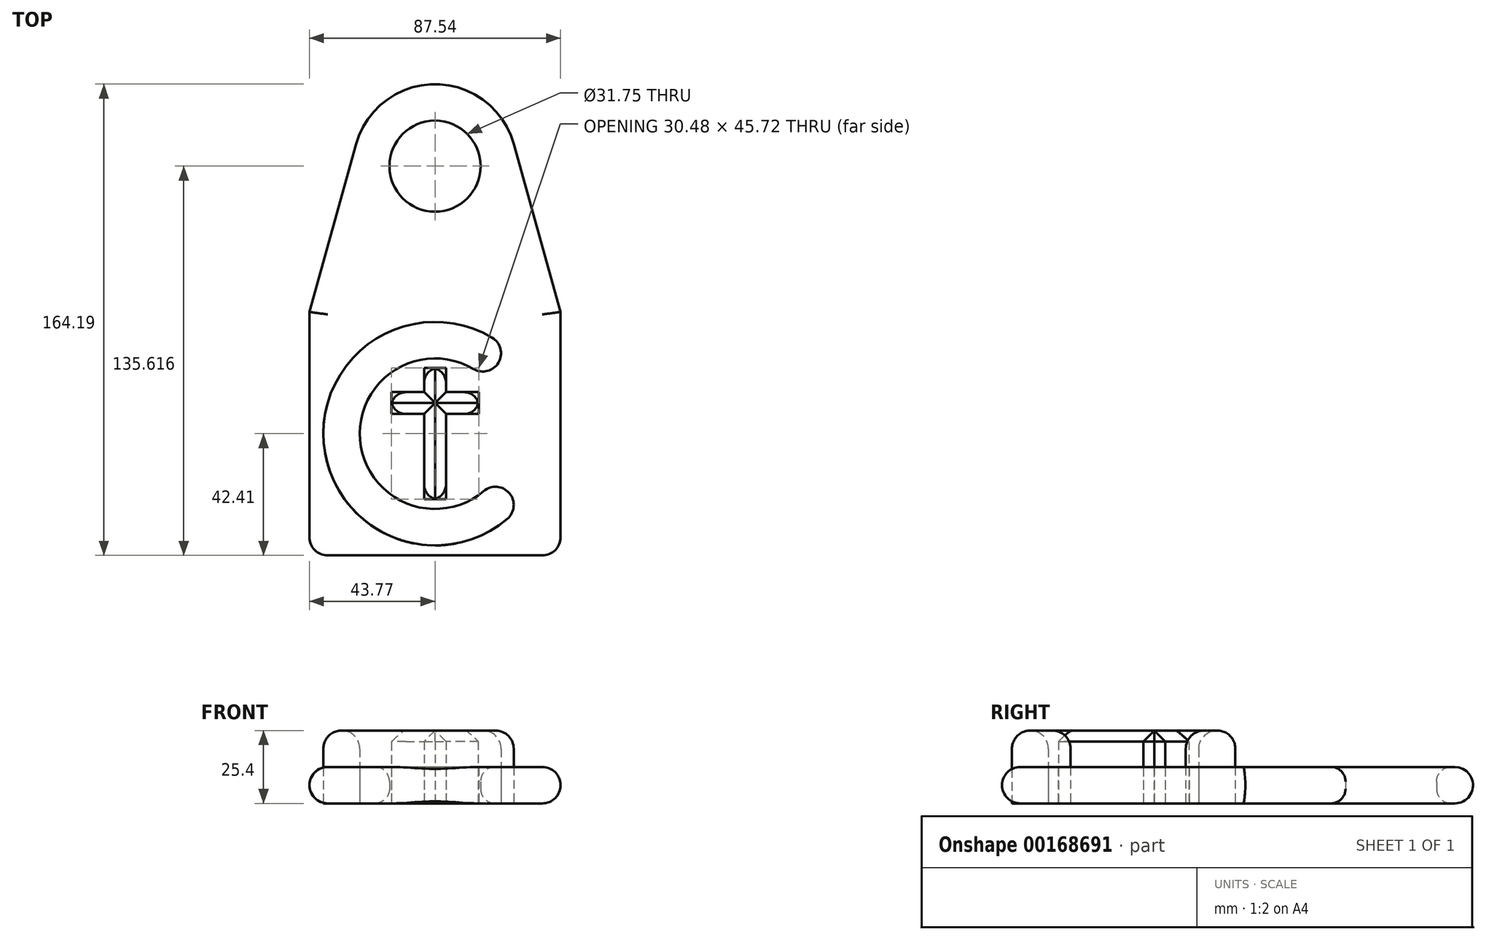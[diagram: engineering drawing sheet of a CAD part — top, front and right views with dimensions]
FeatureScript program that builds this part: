
annotation { "Feature Type Name" : "Feature", "Feature Type Description" : "" }
export const myFeature = defineFeature(function(context is Context, id is Id, definition is map)
    precondition{}
    {
        {
            var Q0;
            Q0=qCreatedBy(makeId("Top.planeOp"),FACE);
            var sketch = newSketch(context, id + "F0", { "sketchPlane" : qUnion([Q0])});
            skLineSegment(sketch, "E0.bottom", {"start": v(-43.77, 42.4) * mm, "end": v(43.77, 42.4) * mm});
            skLineSegment(sketch, "E0.top", {"start": v(-43.77, -42.4) * mm, "end": v(43.77, -42.4) * mm});
            skLineSegment(sketch, "E0.left", {"start": v(-43.77, 42.4) * mm, "end": v(-43.77, -42.4) * mm});
            skLineSegment(sketch, "E0.right", {"start": v(43.77, 42.4) * mm, "end": v(43.77, -42.4) * mm});
            skPoint(sketch, "E0.middle", {"position": v(0, 0) * mm});
            skArc(sketch, "E1", {"start": v(19.9, 33.46) * mm, "mid": v(-38.8, -3.25) * mm, "end": v(25.19, -29.68) * mm});
            skArc(sketch, "E2.0", {"start": v(13.4, 22.54) * mm, "mid": v(-26.14, -2.19) * mm, "end": v(16.97, -20) * mm});
            skLineSegment(sketch, "E3", {"start": v(13.4, 22.54) * mm, "end": v(19.9, 33.46) * mm});
            skLineSegment(sketch, "E4.bottom", {"start": v(-3.81, 22.86) * mm, "end": v(3.8, 22.86) * mm});
            skLineSegment(sketch, "E4.top", {"start": v(-3.8, -22.86) * mm, "end": v(3.81, -22.86) * mm});
            skLineSegment(sketch, "E4.left", {"start": v(-3.81, 22.86) * mm, "end": v(-3.8, -22.86) * mm});
            skLineSegment(sketch, "E4.right", {"start": v(3.8, 22.86) * mm, "end": v(3.81, -22.86) * mm});
            skLineSegment(sketch, "E5", {"start": v(16.97, -20) * mm, "end": v(25.19, -29.68) * mm});
            skLineSegment(sketch, "E6.bottom", {"start": v(-15.24, 14.47) * mm, "end": v(15.24, 14.47) * mm});
            skLineSegment(sketch, "E6.top", {"start": v(-15.24, 6.85) * mm, "end": v(15.24, 6.85) * mm});
            skLineSegment(sketch, "E6.left", {"start": v(-15.24, 14.47) * mm, "end": v(-15.24, 6.85) * mm});
            skLineSegment(sketch, "E6.right", {"start": v(15.24, 14.47) * mm, "end": v(15.24, 6.85) * mm});
            skPoint(sketch, "E6.middle", {"position": v(0, 10.66) * mm});
            skCircle(sketch, "E7", {"center": v(0, 93.2) * mm, "radius": 15.88 * mm});
            skCircle(sketch, "E8.0", {"center": v(0, 93.2) * mm, "radius": 28.58 * mm});
            skLineSegment(sketch, "E9", {"start": v(-43.77, 42.4) * mm, "end": v(-27.53, 100.86) * mm});
            skLineSegment(sketch, "E10.MirrorCS", {"start": v(43.77, 42.4) * mm, "end": v(27.53, 100.86) * mm});
            skArc(sketch, "E11", {"start": v(19.9, 33.46) * mm, "mid": v(22.11, 24.75) * mm, "end": v(13.4, 22.54) * mm});
            skArc(sketch, "E12", {"start": v(16.97, -20) * mm, "mid": v(25.92, -20.73) * mm, "end": v(25.19, -29.68) * mm});
            skSolve(sketch);
        }
        {
            var Q0;
            Q0=makeQuery(id+"F0.imprint","IMPRINT",FACE,{"disambiguationData":[TD([[makeQuery(id+"F0.imprint","IMPRINT",EDGE,{"derivedFrom":sQuery(id+"F0.wireOp",EDGE,"E0.bottom")}),-1.0]])]});
            var Q1;
            Q1=makeQuery(id+"F0.imprint","IMPRINT",FACE,{"disambiguationData":[TD([[makeQuery(id+"F0.imprint","IMPRINT",EDGE,{"derivedFrom":sQuery(id+"F0.wireOp",EDGE,"E0.bottom")}),1.0]])]});
            var Q2;
            Q2=makeQuery(id+"F0.imprint","IMPRINT",FACE,{"disambiguationData":[TD([[makeQuery(id+"F0.imprint","IMPRINT",EDGE,{"derivedFrom":sQuery(id+"F0.wireOp",EDGE,"E7")}),-1.0]])]});
            extrude(context, id + "F1", {"entities" : qUnion([Q0, Q1, Q2]), "depth" : 12.7 * mm, "offsetDistance" : 25.4 * mm});
        }
        {
            var Q0;
            Q0=makeQuery(id+"F0.imprint","IMPRINT",FACE,{"disambiguationData":[TD([[makeQuery(id+"F0.imprint","IMPRINT",EDGE,{"derivedFrom":sQuery(id+"F0.wireOp",EDGE,"E1")}),1.0]])]});
            var Q1;
            {var subQ0=sQuery(id+"F0.wireOp",EDGE,"E6.bottom");var subQ1=sQuery(id+"F0.wireOp",EDGE,"E4.left");var subQ2=makeQuery(id+"F0.imprint","INTERSECT",VERTEX,{"derivedFrom":[subQ1,subQ0]});Q1=makeQuery(id+"F0.imprint","IMPRINT",FACE,{"disambiguationData":[TD([[makeQuery(id+"F0.imprint","IMPRINT",EDGE,{"disambiguationData":[TD([[subQ2,-1.0]])],"derivedFrom":subQ1}),1.0]])]});}
            var Q2;
            {var subQ5=sQuery(id+"F0.wireOp",EDGE,"E6.right");Q2=makeQuery(id+"F0.imprint","IMPRINT",FACE,{"disambiguationData":[TD([[makeQuery(id+"F0.imprint","IMPRINT",EDGE,{"derivedFrom":subQ5}),-1.0]])]});}
            var Q3;
            {var subQ0=sQuery(id+"F0.wireOp",EDGE,"E4.bottom");Q3=makeQuery(id+"F0.imprint","IMPRINT",FACE,{"disambiguationData":[TD([[makeQuery(id+"F0.imprint","IMPRINT",EDGE,{"derivedFrom":subQ0}),-1.0]])]});}
            var Q4;
            {var subQ5=sQuery(id+"F0.wireOp",EDGE,"E6.left");Q4=makeQuery(id+"F0.imprint","IMPRINT",FACE,{"disambiguationData":[TD([[makeQuery(id+"F0.imprint","IMPRINT",EDGE,{"derivedFrom":subQ5}),1.0]])]});}
            var Q5;
            {var subQ0=sQuery(id+"F0.wireOp",EDGE,"E4.top");Q5=makeQuery(id+"F0.imprint","IMPRINT",FACE,{"disambiguationData":[TD([[makeQuery(id+"F0.imprint","IMPRINT",EDGE,{"derivedFrom":subQ0}),1.0]])]});}
            var Q6;
            Q6=makeQuery(id+"F0.imprint","IMPRINT",FACE,{"disambiguationData":[TD([[makeQuery(id+"F0.imprint","IMPRINT",EDGE,{"derivedFrom":sQuery(id+"F0.wireOp",EDGE,"E3")}),-1.0]])]});
            var Q7;
            Q7=makeQuery(id+"F0.imprint","IMPRINT",FACE,{"disambiguationData":[TD([[makeQuery(id+"F0.imprint","IMPRINT",EDGE,{"derivedFrom":sQuery(id+"F0.wireOp",EDGE,"E5")}),1.0]])]});
            extrude(context, id + "F2", {"entities" : qUnion([Q0, Q1, Q2, Q3, Q4, Q5, Q6, Q7]), "depth" : 25.4 * mm, "offsetDistance" : 25.4 * mm});
        }
        {
            var Q0;
            Q0=makeQuery(id+"F1.opExtrude","CAP_EDGE",EDGE,{"disambiguationData":[OSD([sQuery(id+"F0.wireOp",EDGE,"E0.left")])],"isStart":false});
            var Q1;
            Q1=makeQuery(id+"F1.opExtrude","CAP_EDGE",EDGE,{"disambiguationData":[OSD([sQuery(id+"F0.wireOp",EDGE,"E0.top")])],"isStart":false});
            var Q2;
            Q2=makeQuery(id+"F1.opExtrude","SWEPT_EDGE",EDGE,{"disambiguationData":[OSD([sQuery(id+"F0.wireOp",EDGE,"E0.top"),sQuery(id+"F0.wireOp",EDGE,"E0.left")])]});
            var Q3;
            Q3=makeQuery(id+"F1.opExtrude","SWEPT_EDGE",EDGE,{"disambiguationData":[OSD([sQuery(id+"F0.wireOp",EDGE,"E0.top"),sQuery(id+"F0.wireOp",EDGE,"E0.right")])]});
            var Q4;
            Q4=makeQuery(id+"F1.opExtrude","CAP_EDGE",EDGE,{"disambiguationData":[OSD([sQuery(id+"F0.wireOp",EDGE,"E0.right")])],"isStart":false});
            var Q5;
            Q5=makeQuery(id+"F1.opExtrude","CAP_EDGE",EDGE,{"disambiguationData":[OSD([sQuery(id+"F0.wireOp",EDGE,"E10.MirrorCS")])],"isStart":false});
            var Q6;
            Q6=makeQuery(id+"F1.opExtrude","CAP_EDGE",EDGE,{"disambiguationData":[OSD([sQuery(id+"F0.wireOp",EDGE,"E0.right")])],"isStart":true});
            var Q7;
            Q7=makeQuery(id+"F1.opExtrude","CAP_EDGE",EDGE,{"disambiguationData":[OSD([sQuery(id+"F0.wireOp",EDGE,"E10.MirrorCS")])],"isStart":true});
            var Q8;
            Q8=makeQuery(id+"F1.opExtrude","CAP_EDGE",EDGE,{"disambiguationData":[OSD([sQuery(id+"F0.wireOp",EDGE,"E0.top")])],"isStart":true});
            var Q9;
            Q9=makeQuery(id+"F1.opExtrude","CAP_EDGE",EDGE,{"disambiguationData":[OSD([sQuery(id+"F0.wireOp",EDGE,"E0.left")])],"isStart":true});
            var Q10;
            Q10=makeQuery(id+"F1.opExtrude","CAP_EDGE",EDGE,{"disambiguationData":[OSD([sQuery(id+"F0.wireOp",EDGE,"E9")])],"isStart":true});
            fillet(context, id + "F3", {"entities" : qUnion([Q0, Q1, Q2, Q3, Q4, Q5, Q6, Q7, Q8, Q9, Q10]), "radius" : 6.35 * mm, "tangentPropagation" : true, "allowEdgeOverflow" : false});
        }
        {
            var Q0;
            Q0=makeQuery(id+"F1.opExtrude","CAP_EDGE",EDGE,{"disambiguationData":[OSD([sQuery(id+"F0.wireOp",EDGE,"E7")])],"isStart":true});
            var Q1;
            Q1=makeQuery(id+"F1.opExtrude","CAP_EDGE",EDGE,{"disambiguationData":[OSD([sQuery(id+"F0.wireOp",EDGE,"E7")])],"isStart":false});
            fillet(context, id + "F4", {"entities" : qUnion([Q0, Q1]), "radius" : 5.08 * mm, "tangentPropagation" : true, "allowEdgeOverflow" : false});
        }
        {
            var Q0;
            Q0=makeQuery(id+"F2.opExtrude","SWEPT_EDGE",EDGE,{"disambiguationData":[OSD([sQuery(id+"F0.wireOp",EDGE,"E6.bottom"),sQuery(id+"F0.wireOp",EDGE,"E6.right")])]});
            var Q1;
            Q1=makeQuery(id+"F2.opExtrude","SWEPT_EDGE",EDGE,{"disambiguationData":[OSD([sQuery(id+"F0.wireOp",EDGE,"E4.bottom"),sQuery(id+"F0.wireOp",EDGE,"E4.right")])]});
            var Q2;
            Q2=makeQuery(id+"F2.opExtrude","SWEPT_EDGE",EDGE,{"disambiguationData":[OSD([sQuery(id+"F0.wireOp",EDGE,"E4.bottom"),sQuery(id+"F0.wireOp",EDGE,"E4.left")])]});
            var Q3;
            Q3=makeQuery(id+"F2.opExtrude","SWEPT_EDGE",EDGE,{"disambiguationData":[OSD([sQuery(id+"F0.wireOp",EDGE,"E6.bottom"),sQuery(id+"F0.wireOp",EDGE,"E6.left")])]});
            var Q4;
            Q4=makeQuery(id+"F2.opExtrude","SWEPT_EDGE",EDGE,{"disambiguationData":[OSD([sQuery(id+"F0.wireOp",EDGE,"E6.top"),sQuery(id+"F0.wireOp",EDGE,"E6.left")])]});
            var Q5;
            Q5=makeQuery(id+"F2.opExtrude","SWEPT_EDGE",EDGE,{"disambiguationData":[OSD([sQuery(id+"F0.wireOp",EDGE,"E4.top"),sQuery(id+"F0.wireOp",EDGE,"E4.left")])]});
            var Q6;
            Q6=makeQuery(id+"F2.opExtrude","SWEPT_EDGE",EDGE,{"disambiguationData":[OSD([sQuery(id+"F0.wireOp",EDGE,"E4.top"),sQuery(id+"F0.wireOp",EDGE,"E4.right")])]});
            var Q7;
            Q7=makeQuery(id+"F2.opExtrude","SWEPT_EDGE",EDGE,{"disambiguationData":[OSD([sQuery(id+"F0.wireOp",EDGE,"E6.top"),sQuery(id+"F0.wireOp",EDGE,"E6.right")])]});
            fillet(context, id + "F5", {"entities" : qUnion([Q0, Q1, Q2, Q3, Q4, Q5, Q6, Q7]), "radius" : 5.08 * mm, "tangentPropagation" : true, "allowEdgeOverflow" : false});
        }
        {
            var Q0;
            Q0=makeQuery(id+"F2.opExtrude","CAP_EDGE",EDGE,{"disambiguationData":[OSD([sQuery(id+"F0.wireOp",EDGE,"E1")])],"isStart":false});
            var Q1;
            Q1=makeQuery(id+"F2.opExtrude","CAP_EDGE",EDGE,{"disambiguationData":[OSD([sQuery(id+"F0.wireOp",EDGE,"E2.0")])],"isStart":false});
            fillet(context, id + "F6", {"entities" : qUnion([Q0, Q1]), "radius" : 6.35 * mm, "tangentPropagation" : true, "allowEdgeOverflow" : false});
        }
        {
            var Q0;
            {var subQ0=sQuery(id+"F0.wireOp",EDGE,"E6.top");Q0=makeQuery(id+"F2.opExtrude","CAP_EDGE",EDGE,{"disambiguationData":[OSD([subQ0]),TDD([makeQuery(id+"F0.imprint","IMPRINT",EDGE,{"disambiguationData":[TD([[makeQuery(id+"F0.imprint","INTERSECT",VERTEX,{"derivedFrom":[subQ0,sQuery(id+"F0.wireOp",EDGE,"E6.left")]}),-1.0]])],"derivedFrom":subQ0})])],"isStart":false});}
            var Q1;
            {var subQ0=sQuery(id+"F0.wireOp",EDGE,"E6.bottom");Q1=makeQuery(id+"F2.opExtrude","CAP_EDGE",EDGE,{"disambiguationData":[OSD([subQ0]),TDD([makeQuery(id+"F0.imprint","IMPRINT",EDGE,{"disambiguationData":[TD([[makeQuery(id+"F0.imprint","INTERSECT",VERTEX,{"derivedFrom":[subQ0,sQuery(id+"F0.wireOp",EDGE,"E6.left")]}),-1.0]])],"derivedFrom":subQ0})])],"isStart":false});}
            var Q2;
            {var subQ0=sQuery(id+"F0.wireOp",EDGE,"E4.left");Q2=makeQuery(id+"F2.opExtrude","CAP_EDGE",EDGE,{"disambiguationData":[OSD([subQ0]),TDD([makeQuery(id+"F0.imprint","IMPRINT",EDGE,{"disambiguationData":[TD([[makeQuery(id+"F0.imprint","INTERSECT",VERTEX,{"derivedFrom":[sQuery(id+"F0.wireOp",EDGE,"E4.bottom"),subQ0]}),-1.0]])],"derivedFrom":subQ0})])],"isStart":false});}
            var Q3;
            {var subQ0=sQuery(id+"F0.wireOp",EDGE,"E4.right");Q3=makeQuery(id+"F2.opExtrude","CAP_EDGE",EDGE,{"disambiguationData":[OSD([subQ0]),TDD([makeQuery(id+"F0.imprint","IMPRINT",EDGE,{"disambiguationData":[TD([[makeQuery(id+"F0.imprint","INTERSECT",VERTEX,{"derivedFrom":[sQuery(id+"F0.wireOp",EDGE,"E4.bottom"),subQ0]}),-1.0]])],"derivedFrom":subQ0})])],"isStart":false});}
            var Q4;
            {var subQ0=sQuery(id+"F0.wireOp",EDGE,"E6.bottom");Q4=makeQuery(id+"F2.opExtrude","CAP_EDGE",EDGE,{"disambiguationData":[OSD([subQ0]),TDD([makeQuery(id+"F0.imprint","IMPRINT",EDGE,{"disambiguationData":[TD([[makeQuery(id+"F0.imprint","INTERSECT",VERTEX,{"derivedFrom":[subQ0,sQuery(id+"F0.wireOp",EDGE,"E6.right")]}),1.0]])],"derivedFrom":subQ0})])],"isStart":false});}
            var Q5;
            {var subQ0=sQuery(id+"F0.wireOp",EDGE,"E6.top");Q5=makeQuery(id+"F2.opExtrude","CAP_EDGE",EDGE,{"disambiguationData":[OSD([subQ0]),TDD([makeQuery(id+"F0.imprint","IMPRINT",EDGE,{"disambiguationData":[TD([[makeQuery(id+"F0.imprint","INTERSECT",VERTEX,{"derivedFrom":[subQ0,sQuery(id+"F0.wireOp",EDGE,"E6.right")]}),1.0]])],"derivedFrom":subQ0})])],"isStart":false});}
            var Q6;
            {var subQ0=sQuery(id+"F0.wireOp",EDGE,"E4.right");Q6=makeQuery(id+"F2.opExtrude","CAP_EDGE",EDGE,{"disambiguationData":[OSD([subQ0]),TDD([makeQuery(id+"F0.imprint","IMPRINT",EDGE,{"disambiguationData":[TD([[makeQuery(id+"F0.imprint","INTERSECT",VERTEX,{"derivedFrom":[sQuery(id+"F0.wireOp",EDGE,"E4.top"),subQ0]}),1.0]])],"derivedFrom":subQ0})])],"isStart":false});}
            var Q7;
            {var subQ0=sQuery(id+"F0.wireOp",EDGE,"E4.left");Q7=makeQuery(id+"F2.opExtrude","CAP_EDGE",EDGE,{"disambiguationData":[OSD([subQ0]),TDD([makeQuery(id+"F0.imprint","IMPRINT",EDGE,{"disambiguationData":[TD([[makeQuery(id+"F0.imprint","INTERSECT",VERTEX,{"derivedFrom":[sQuery(id+"F0.wireOp",EDGE,"E4.top"),subQ0]}),1.0]])],"derivedFrom":subQ0})])],"isStart":false});}
            chamfer(context, id + "F7", {"entities" : qUnion([Q0, Q1, Q2, Q3, Q4, Q5, Q6, Q7]), "width" : 3.8 * mm, "tangentPropagation" : true});
        }
    });
